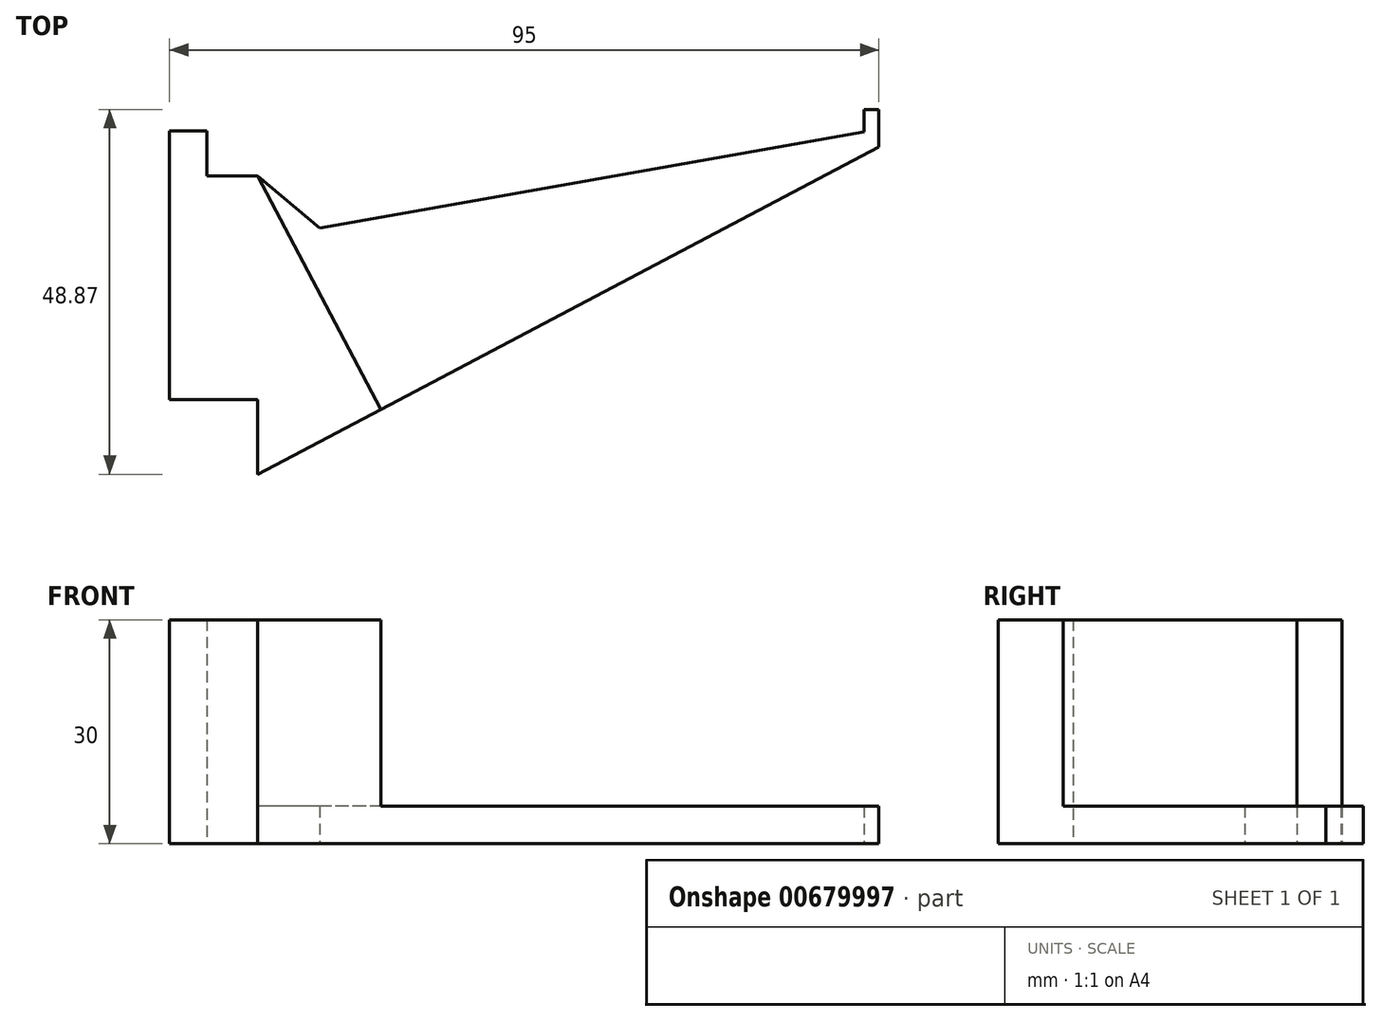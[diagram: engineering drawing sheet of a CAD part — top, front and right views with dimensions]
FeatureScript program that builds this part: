
annotation { "Feature Type Name" : "Feature", "Feature Type Description" : "" }
export const myFeature = defineFeature(function(context is Context, id is Id, definition is map)
    precondition{}
    {
        {
            var Q0;
            Q0=qCreatedBy(makeId("Top.planeOp"),FACE);
            var sketch = newSketch(context, id + "F0", { "sketchPlane" : qUnion([Q0])});
            skLineSegment(sketch, "E0", {"start": v(0, 0) * mm, "end": v(0, 36) * mm});
            skLineSegment(sketch, "E1", {"start": v(0, 36) * mm, "end": v(5, 36) * mm});
            skLineSegment(sketch, "E2", {"start": v(5, 36) * mm, "end": v(5, 30) * mm});
            skLineSegment(sketch, "E3", {"start": v(5, 30) * mm, "end": v(11.8, 30) * mm});
            skLineSegment(sketch, "E4", {"start": v(0, 0) * mm, "end": v(5, 0) * mm});
            skLineSegment(sketch, "E5", {"start": v(5, 0) * mm, "end": v(11.8, 0) * mm});
            skLineSegment(sketch, "E6", {"start": v(11.8, 0) * mm, "end": v(11.8, -10) * mm});
            skLineSegment(sketch, "E7", {"start": v(11.8, -10) * mm, "end": v(95, 33.87) * mm});
            skLineSegment(sketch, "E8", {"start": v(95, 33.87) * mm, "end": v(95, 38.87) * mm});
            skLineSegment(sketch, "E9", {"start": v(93, 38.87) * mm, "end": v(95, 38.87) * mm});
            skLineSegment(sketch, "E10", {"start": v(93, 38.87) * mm, "end": v(93, 35.87) * mm});
            skLineSegment(sketch, "E11", {"start": v(93, 35.87) * mm, "end": v(20.12, 23.02) * mm});
            skLineSegment(sketch, "E12", {"start": v(20.12, 23.02) * mm, "end": v(11.8, 30) * mm});
            skLineSegment(sketch, "E13", {"start": v(11.8, 30) * mm, "end": v(28.3, -1.3) * mm});
            skSolve(sketch);
        }
        {
            var Q0;
            Q0=qSketchRegion(id+"F0",true);
            extrude(context, id + "F1", {"entities" : qUnion([Q0]), "depth" : 5 * mm});
        }
        {
            var Q0;
            Q0=makeQuery(id+"F0.imprint","IMPRINT",FACE,{"disambiguationData":[TD([[makeQuery(id+"F0.imprint","IMPRINT",EDGE,{"derivedFrom":sQuery(id+"F0.wireOp",EDGE,"E0")}),-1.0]])]});
            extrude(context, id + "F2", {"entities" : qUnion([Q0]), "operationType" : NewBodyOperationType.ADD, "depth" : 30 * mm});
        }
    });
